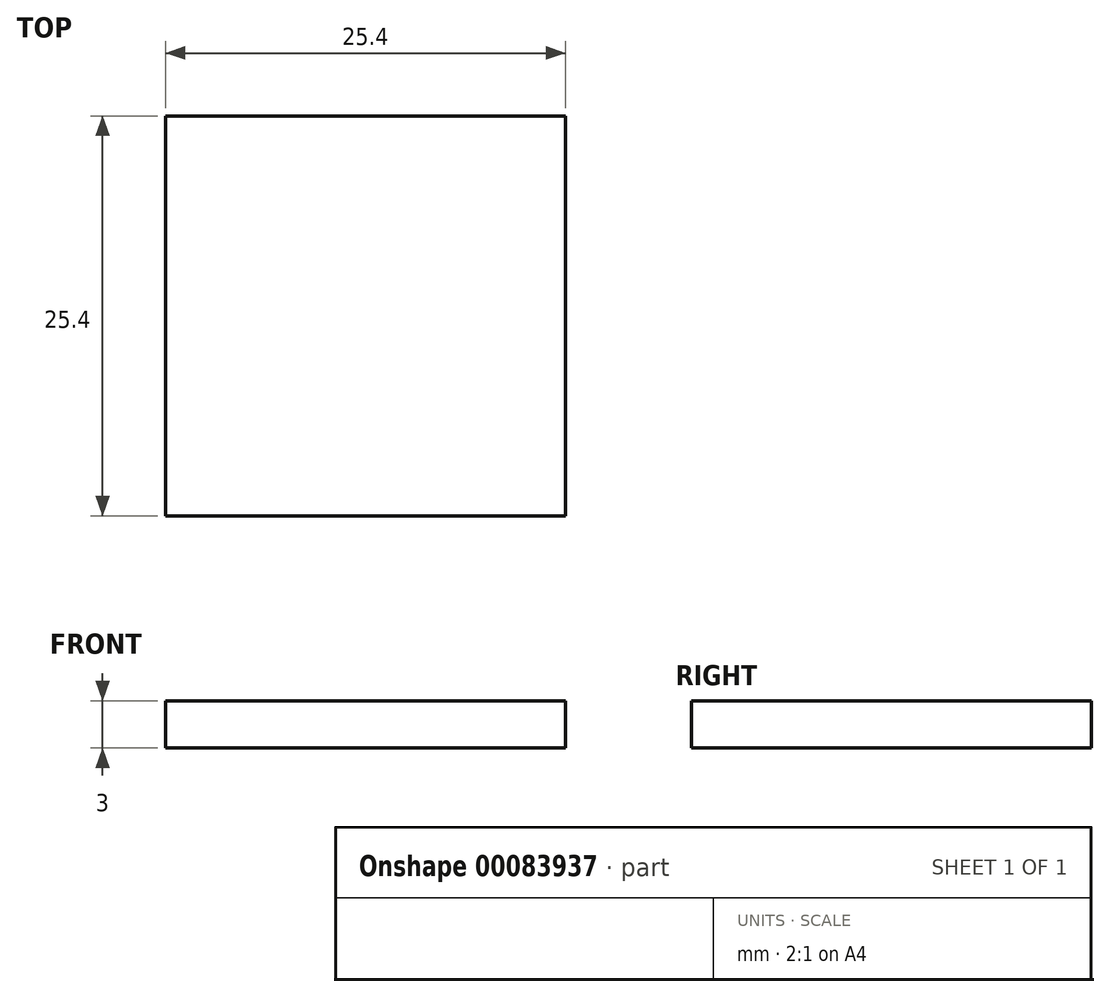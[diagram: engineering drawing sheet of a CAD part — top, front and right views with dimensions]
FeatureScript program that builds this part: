
annotation { "Feature Type Name" : "Feature", "Feature Type Description" : "" }
export const myFeature = defineFeature(function(context is Context, id is Id, definition is map)
    precondition{}
    {
        {
            var Q0;
            Q0=qCreatedBy(makeId("Top.planeOp"),FACE);
            var sketch = newSketch(context, id + "F0", { "sketchPlane" : qUnion([Q0])});
            skLineSegment(sketch, "E0.bottom", {"start": v(-12.7, 12.7) * mm, "end": v(12.7, 12.7) * mm});
            skLineSegment(sketch, "E0.top", {"start": v(-12.7, -12.7) * mm, "end": v(12.7, -12.7) * mm});
            skLineSegment(sketch, "E0.left", {"start": v(-12.7, 12.7) * mm, "end": v(-12.7, -12.7) * mm});
            skLineSegment(sketch, "E0.right", {"start": v(12.7, 12.7) * mm, "end": v(12.7, -12.7) * mm});
            skPoint(sketch, "E0.middle", {"position": v(0, 0) * mm});
            skSolve(sketch);
        }
        {
            var Q0;
            Q0 = qSketchRegion(id + "F0", true);
            extrude(context, id + "F1", {"entities" : qUnion([Q0]), "depth" : 3 * mm});
        }
    });
